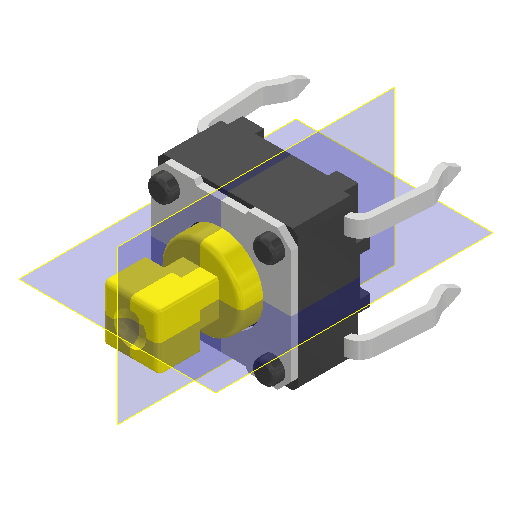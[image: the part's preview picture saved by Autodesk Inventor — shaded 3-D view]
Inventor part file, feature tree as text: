
AUTODESK INVENTOR PART (.ipt)
format: ipt  version: 2025 (Build 290162000, 162)  size: 346,112 bytes
history: native  units: in
note: dims shown in document units (in); Inventor stores cm internally (conversion verified against a paired STEP export)
features: plane x2, imported_body x1
ambient origin geometry x8: Origin, YZ Plane, XZ Plane, XY Plane, X Axis, Y Axis, Z Axis, Center Point
bodies: Solid1 (feature_tree)
feature tree (3):
  plane  "Work Plane4"
  plane  "Work Plane5"
  imported_body  "Base1"
